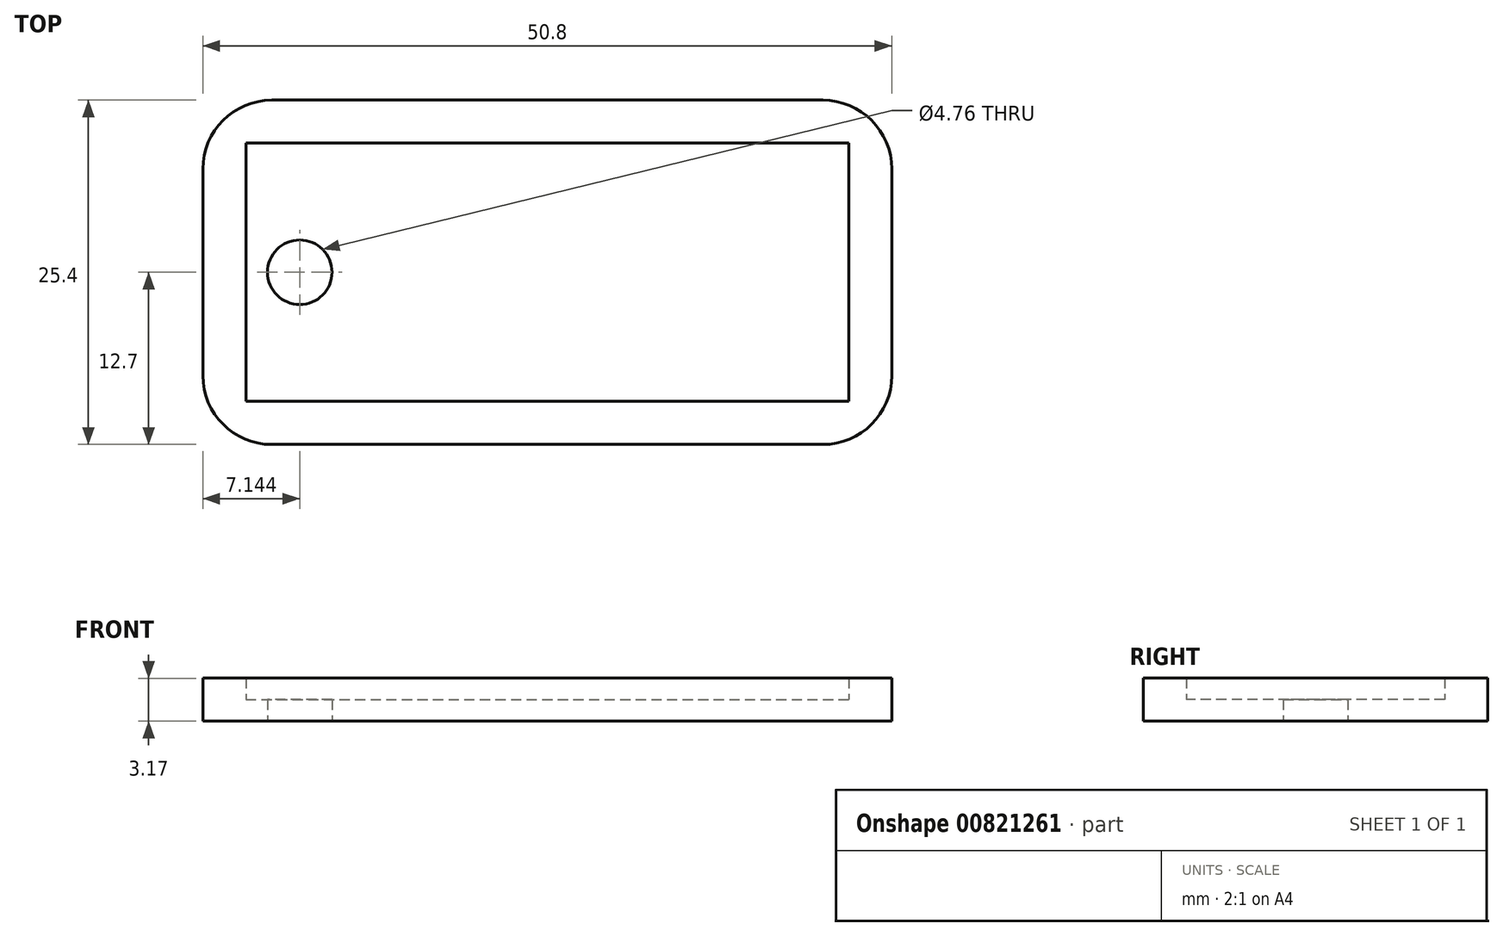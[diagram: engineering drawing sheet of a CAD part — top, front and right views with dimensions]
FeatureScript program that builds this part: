
annotation { "Feature Type Name" : "Feature", "Feature Type Description" : "" }
export const myFeature = defineFeature(function(context is Context, id is Id, definition is map)
    precondition{}
    {
        {
            var Q0;
            Q0=qCreatedBy(makeId("Top.planeOp"),FACE);
            var sketch = newSketch(context, id + "F0", { "sketchPlane" : qUnion([Q0])});
            skLineSegment(sketch, "E0.bottom", {"start": v(0, 0) * mm, "end": v(50.8, 0) * mm});
            skLineSegment(sketch, "E0.top", {"start": v(0, 25.4) * mm, "end": v(50.8, 25.4) * mm});
            skLineSegment(sketch, "E0.left", {"start": v(0, 0) * mm, "end": v(0, 25.4) * mm});
            skLineSegment(sketch, "E0.right", {"start": v(50.8, 0) * mm, "end": v(50.8, 25.4) * mm});
            skPoint(sketch, "E1.centerSnap0", {"position": v(0, 12.7) * mm});
            skCircle(sketch, "E2", {"center": v(7.14, 12.7) * mm, "radius": 2.38 * mm});
            skLineSegment(sketch, "E3.bottom", {"start": v(3.17, 22.23) * mm, "end": v(47.63, 22.23) * mm});
            skLineSegment(sketch, "E3.top", {"start": v(3.18, 3.18) * mm, "end": v(47.63, 3.18) * mm});
            skLineSegment(sketch, "E3.left", {"start": v(3.17, 22.23) * mm, "end": v(3.18, 3.18) * mm});
            skLineSegment(sketch, "E3.right", {"start": v(47.63, 22.23) * mm, "end": v(47.63, 3.18) * mm});
            skSolve(sketch);
        }
        {
            var Q0;
            Q0=makeQuery(id+"F0.imprint","IMPRINT",FACE,{"disambiguationData":[TD([[makeQuery(id+"F0.imprint","IMPRINT",EDGE,{"derivedFrom":sQuery(id+"F0.wireOp",EDGE,"E2")}),-1.0]])]});
            extrude(context, id + "F1", {"entities" : qUnion([Q0]), "depth" : 1.59 * mm, "offsetDistance" : 25.4 * mm});
        }
        {
            var Q0;
            Q0 = qSketchRegion(id + "F0", true);
            extrude(context, id + "F2", {"entities" : qUnion([Q0]), "operationType" : NewBodyOperationType.ADD, "depth" : 3.17 * mm, "offsetDistance" : 25.4 * mm});
        }
        {
            var Q0;
            Q0=makeQuery(id+"F2.opExtrude","SWEPT_EDGE",EDGE,{"disambiguationData":[OSD([sQuery(id+"F0.wireOp",EDGE,"E0.bottom"),sQuery(id+"F0.wireOp",EDGE,"E0.right")])]});
            var Q1;
            Q1=makeQuery(id+"F2.opExtrude","SWEPT_EDGE",EDGE,{"disambiguationData":[OSD([sQuery(id+"F0.wireOp",EDGE,"E0.top"),sQuery(id+"F0.wireOp",EDGE,"E0.right")])]});
            var Q2;
            Q2=makeQuery(id+"F2.opExtrude","SWEPT_EDGE",EDGE,{"disambiguationData":[OSD([sQuery(id+"F0.wireOp",EDGE,"E0.bottom"),sQuery(id+"F0.wireOp",EDGE,"E0.left")])]});
            var Q3;
            Q3=makeQuery(id+"F2.opExtrude","SWEPT_EDGE",EDGE,{"disambiguationData":[OSD([sQuery(id+"F0.wireOp",EDGE,"E0.top"),sQuery(id+"F0.wireOp",EDGE,"E0.left")])]});
            fillet(context, id + "F3", {"entities" : qUnion([Q0, Q1, Q2, Q3]), "radius" : 5.08 * mm, "tangentPropagation" : true, "allowEdgeOverflow" : false});
        }
    });
